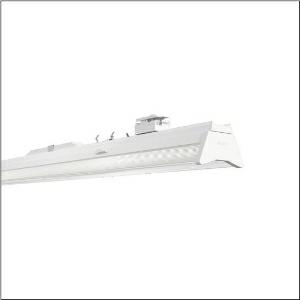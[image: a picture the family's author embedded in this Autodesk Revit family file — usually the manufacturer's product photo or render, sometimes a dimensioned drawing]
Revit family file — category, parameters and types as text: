
# Revit family: licross_r__11_performance_mo_51td167n485g_c044
name_source: partatom
category: Lighting Fixtures
units: mm (PartAtom-declared; Revit-internal decimal feet)

## family parameters
Cut with Voids When Loaded = No
Host = Face
Light Source = No
Part Type = Normal
Room Calculation Point = No
Round Connector Dimension = Use Diameter
Shared = No

## types (1)
- Licross® 11 Performance MO (1 x LED, 8840 lm, 48.6 W, 4000K)
    Apparent Load = 49 VA
    CIE Flux Codes = 66 88 96 79 100
    Color Rendering = 80
    Color Temperature = 4000K
    Default Elevation = 1800 mm
    Description = Licross® 11 Performance MO, luminaire insert, of sheet steel, galvanised, coil coated, white, length: 1.500mm, width: 120mm, height: 123mm, LED rated luminous flux: 8.840lm, light colour: 840, control gear: ON/OFF, with plug, 3-pole, with phase selection, mains connection: 220..240V, AC, 50/60Hz, rated input power: 49W, internal wiring halogen-free, primary light control with lens, of plastic, primary optical cover: cover, of PMMA, light emission: direct/indirect distribution, primary light characteristic: symmetric, protection rating (complete): IP54, insulation class (complete): insulation class I (protective earthing), certification: CE, ENEC, VDE, UKCA, protection symbol: D if used in an environment with non-conductive dust loads with corresponding accessories, impact resistance: IK06, permissible ambient temperature for indoor applications: -25..+35°C, corresponds to IFS (International Featured Standards) requirements for safety and quality in the food industry, reducing of maximum allowable ambient temperature of 5°C with ceiling mounting, LABS conformity tested according to VDMA 24364:2018-05, packaging unit: 1 piece
    Height = 114 mm
    Lamp = 1 x LED
    Lamp Light Flux = 8840 lm
    Lamp Power = 48.6 W
    Lamp count = 1
    Length = 1500 mm
    Luminous efficacy = 182 lm/W
    Manufacturer = Siteco
    ModVariant = No
    Model = 51TD167N485G
    Mounting Place = Ceiling
    Mounting Type = Pendant
    Number of Poles = 1
    OnlyDefault = Yes
    Power Factor = 1
    Product Name = Licross® 11 Performance MO
    Product group = luminaire insert | ceiling pendant
    ProductGroupID = 902
    Protection Class = Protection class I
    Protection Degree = IP 54
    RLX_Detail_Level = 1
    RLX_Emergency_Light_Flux = 0 lm
    RLX_Emergency_Type = 0
    RLX_Emergency_Type_DB = No
    RlxData = <blob elided: 30397 chars, md5=ead6a062>
    Socket = socket
    Standby Power = 0 W
    System Light Flux = 8840 lm
    System Power = 49 W
    Type Comments = Product without accessories
    Type Image = l_1256138.jpg
    URL = http://relux.com
    VarID = ---
    Voltage = 0 V
    Weight = 0.00 kg
    Width = 120 mm

## geometry (parser evidence)
native form markers: Blend x4, Sweep x12
no freeform markers — native parametric forms only
